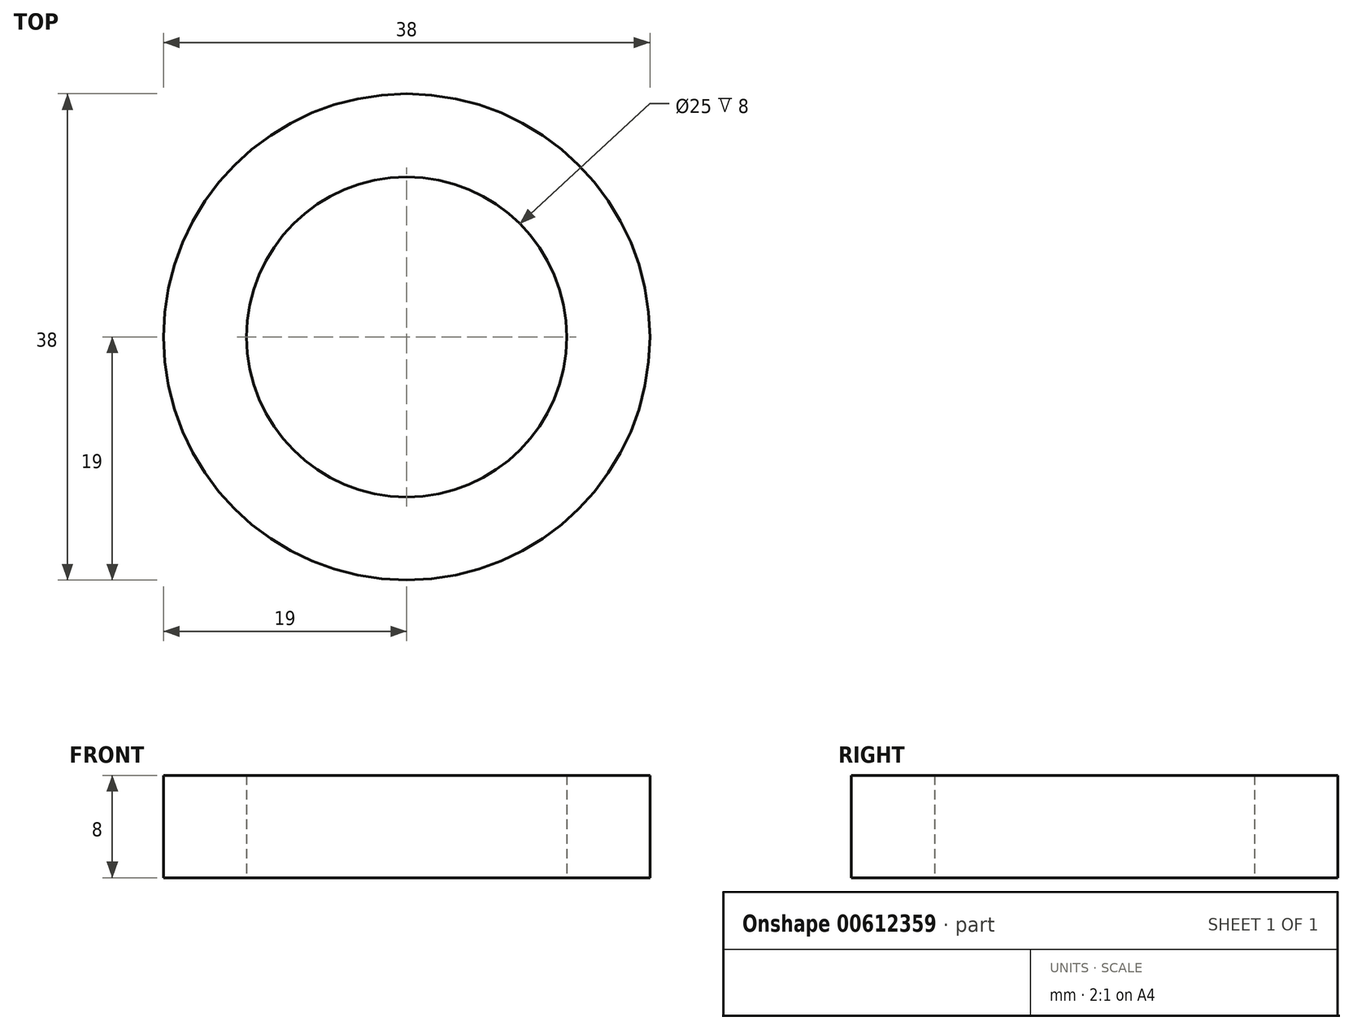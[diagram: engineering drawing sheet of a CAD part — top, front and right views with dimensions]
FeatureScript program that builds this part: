
annotation { "Feature Type Name" : "Feature", "Feature Type Description" : "" }
export const myFeature = defineFeature(function(context is Context, id is Id, definition is map)
    precondition{}
    {
        {
            var Q0;
            Q0=qCreatedBy(makeId("Front.planeOp"),FACE);
            var sketch = newSketch(context, id + "F0", { "sketchPlane" : qUnion([Q0])});
            skLineSegment(sketch, "E0.bottom", {"start": v(12.5, 0) * mm, "end": v(19, 0) * mm});
            skLineSegment(sketch, "E0.top", {"start": v(12.5, 8) * mm, "end": v(19, 8) * mm});
            skLineSegment(sketch, "E0.left", {"start": v(12.5, 0) * mm, "end": v(12.5, 8) * mm});
            skLineSegment(sketch, "E0.right", {"start": v(19, 0) * mm, "end": v(19, 8) * mm});
            skLineSegment(sketch, "E1", {"start": v(0, 0) * mm, "end": v(0, 16.06) * mm});
            skSolve(sketch);
        }
        {
            var Q0;
            Q0=makeQuery(id+"F0.imprint","IMPRINT",FACE,{"disambiguationData":[TD([[makeQuery(id+"F0.imprint","IMPRINT",EDGE,{"derivedFrom":sQuery(id+"F0.wireOp",EDGE,"E0.bottom")}),1.0]])]});
            var Q1;
            Q1=sQuery(id+"F0.wireOp",EDGE,"E1");
            revolve(context, id + "F1", {"entities" : qUnion([Q0]), "axis" : qUnion([Q1]), "revolveType" : RevolveType.FULL});
        }
    });
